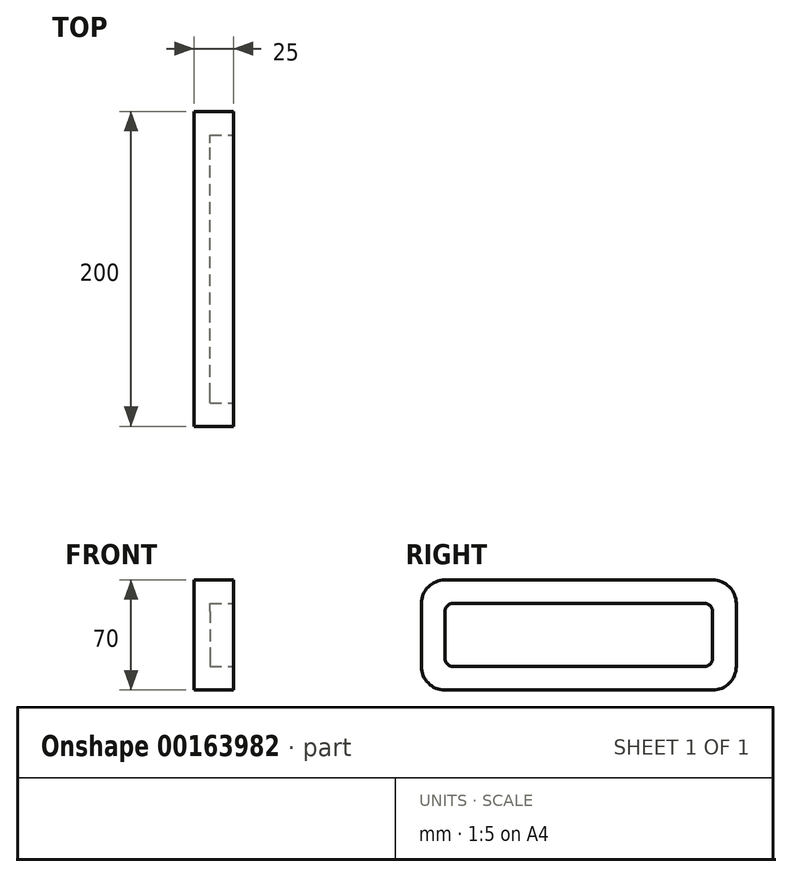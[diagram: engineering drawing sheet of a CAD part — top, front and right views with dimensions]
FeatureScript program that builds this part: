
annotation { "Feature Type Name" : "Feature", "Feature Type Description" : "" }
export const myFeature = defineFeature(function(context is Context, id is Id, definition is map)
    precondition{}
    {
        {
            var Q0;
            Q0=qCreatedBy(makeId("Right.planeOp"),FACE);
            var sketch = newSketch(context, id + "F0", { "sketchPlane" : qUnion([Q0])});
            skLineSegment(sketch, "E0.bottom", {"start": v(-85.95, 73.62) * mm, "end": v(84.05, 73.62) * mm});
            skLineSegment(sketch, "E0.top", {"start": v(-85.95, 3.62) * mm, "end": v(84.05, 3.62) * mm});
            skLineSegment(sketch, "E0.left", {"start": v(-100.95, 58.62) * mm, "end": v(-100.95, 18.62) * mm});
            skLineSegment(sketch, "E0.right", {"start": v(99.05, 58.62) * mm, "end": v(99.05, 18.62) * mm});
            skPoint(sketch, "E1.visualSharp", {"position": v(-100.95, 73.62) * mm});
            skArc(sketch, "E1.filletArc", {"start": v(-85.95, 73.62) * mm, "mid": v(-96.55, 69.23) * mm, "end": v(-100.95, 58.62) * mm});
            skPoint(sketch, "E2.visualSharp", {"position": v(-100.95, 3.62) * mm});
            skArc(sketch, "E2.filletArc", {"start": v(-100.95, 18.62) * mm, "mid": v(-96.55, 8.01) * mm, "end": v(-85.95, 3.62) * mm});
            skPoint(sketch, "E3.visualSharp", {"position": v(99.05, 3.62) * mm});
            skArc(sketch, "E3.filletArc", {"start": v(84.05, 3.62) * mm, "mid": v(94.66, 8.01) * mm, "end": v(99.05, 18.62) * mm});
            skPoint(sketch, "E4.visualSharp", {"position": v(99.05, 73.62) * mm});
            skArc(sketch, "E4.filletArc", {"start": v(99.05, 58.62) * mm, "mid": v(94.66, 69.23) * mm, "end": v(84.05, 73.62) * mm});
            skSolve(sketch);
        }
        {
            var Q0;
            Q0=makeQuery(id+"F0.imprint","IMPRINT",FACE,{"disambiguationData":[TD([[makeQuery(id+"F0.imprint","IMPRINT",EDGE,{"derivedFrom":sQuery(id+"F0.wireOp",EDGE,"E0.bottom")}),-1.0]])]});
            extrude(context, id + "F1", {"entities" : qUnion([Q0]), "depth" : 25 * mm});
        }
        {
            var Q0;
            Q0=makeQuery(id+"F1.opExtrude","CAP_FACE",FACE,{"disambiguationData":[OSD([sQuery(id+"F0.wireOp",EDGE,"E0.bottom"),sQuery(id+"F0.wireOp",EDGE,"E0.top"),sQuery(id+"F0.wireOp",EDGE,"E0.left"),sQuery(id+"F0.wireOp",EDGE,"E0.right"),sQuery(id+"F0.wireOp",EDGE,"E1.filletArc"),sQuery(id+"F0.wireOp",EDGE,"E2.filletArc"),sQuery(id+"F0.wireOp",EDGE,"E3.filletArc"),sQuery(id+"F0.wireOp",EDGE,"E4.filletArc")])],"isStart":false});
            var sketch = newSketch(context, id + "F2", { "sketchPlane" : qUnion([Q0])});
            skLineSegment(sketch, "E5.bottom", {"start": v(-80.95, 58.62) * mm, "end": v(79.05, 58.62) * mm});
            skLineSegment(sketch, "E5.top", {"start": v(-80.95, 18.62) * mm, "end": v(79.05, 18.62) * mm});
            skLineSegment(sketch, "E5.left", {"start": v(-85.95, 53.62) * mm, "end": v(-85.95, 23.62) * mm});
            skLineSegment(sketch, "E5.right", {"start": v(84.05, 53.62) * mm, "end": v(84.05, 23.62) * mm});
            skPoint(sketch, "E6.visualSharp", {"position": v(-85.95, 58.62) * mm});
            skArc(sketch, "E6.filletArc", {"start": v(-80.95, 58.62) * mm, "mid": v(-84.48, 57.16) * mm, "end": v(-85.95, 53.62) * mm});
            skPoint(sketch, "E7.visualSharp", {"position": v(-85.95, 18.62) * mm});
            skArc(sketch, "E7.filletArc", {"start": v(-85.95, 23.62) * mm, "mid": v(-84.48, 20.09) * mm, "end": v(-80.95, 18.62) * mm});
            skPoint(sketch, "E8.visualSharp", {"position": v(84.05, 18.62) * mm});
            skArc(sketch, "E8.filletArc", {"start": v(79.05, 18.62) * mm, "mid": v(82.59, 20.09) * mm, "end": v(84.05, 23.62) * mm});
            skPoint(sketch, "E9.visualSharp", {"position": v(84.05, 58.62) * mm});
            skArc(sketch, "E9.filletArc", {"start": v(84.05, 53.62) * mm, "mid": v(82.59, 57.16) * mm, "end": v(79.05, 58.62) * mm});
            skSolve(sketch);
        }
        {
            var Q0;
            Q0=makeQuery(id+"F2.imprint","IMPRINT",FACE,{"disambiguationData":[TD([[makeQuery(id+"F2.imprint","IMPRINT",EDGE,{"derivedFrom":sQuery(id+"F2.wireOp",EDGE,"E5.bottom")}),-1.0]])]});
            extrude(context, id + "F3", {"entities" : qUnion([Q0]), "operationType" : NewBodyOperationType.REMOVE, "oppositeDirection" : true, "depth" : 15 * mm});
        }
    });
